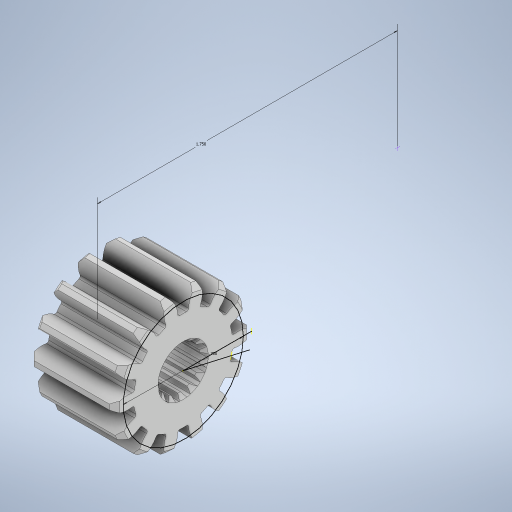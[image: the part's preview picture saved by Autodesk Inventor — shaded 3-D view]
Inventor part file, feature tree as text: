
AUTODESK INVENTOR PART (.ipt)
format: ipt  version: 2023 (Build 270158030, 158C)  size: 587,264 bytes
history: native  units: in
note: dims shown in document units (in); Inventor stores cm internally (conversion verified against a paired STEP export)
features: sketch x2, pattern_circular x1
ambient origin geometry x8: Origin, YZ Plane, XZ Plane, XY Plane, X Axis, Y Axis, Z Axis, Center Point
bodies: Solid1 (feature_tree)
feature tree (3):
  sketch  "Sketch1"  dims[d0=0.7in]
  sketch  "Sketch2"  dims[d2=1.75in]
  pattern_circular  "CirPattern1"
